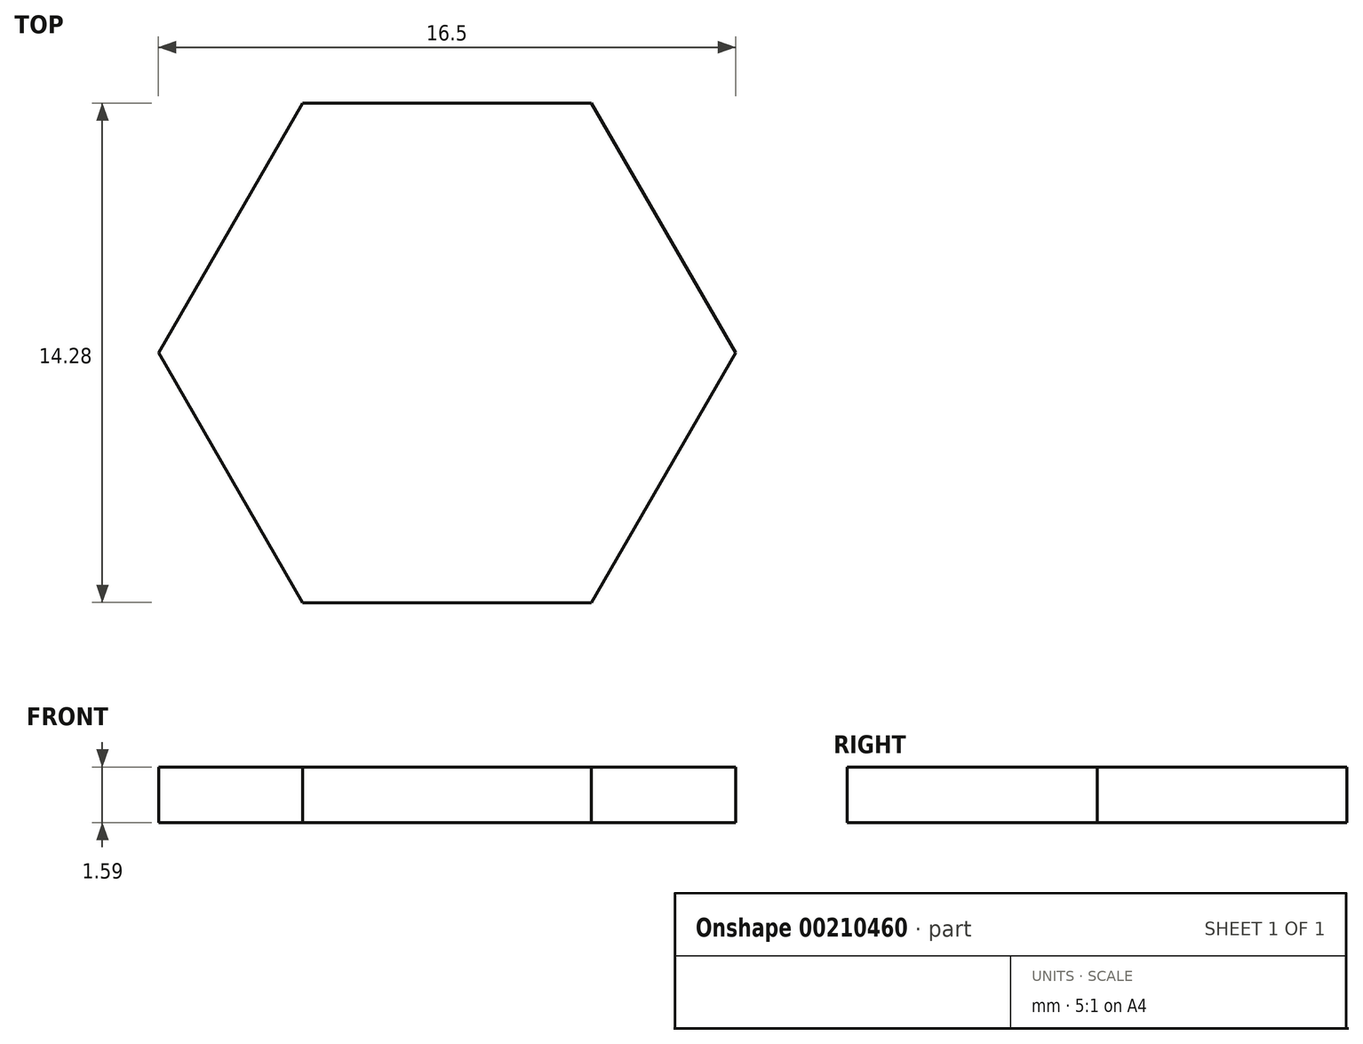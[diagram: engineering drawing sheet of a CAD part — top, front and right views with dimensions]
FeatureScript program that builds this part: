
annotation { "Feature Type Name" : "Feature", "Feature Type Description" : "" }
export const myFeature = defineFeature(function(context is Context, id is Id, definition is map)
    precondition{}
    {
        {
            var Q0;
            Q0=qCreatedBy(makeId("Top.planeOp"),FACE);
            var sketch = newSketch(context, id + "F0", { "sketchPlane" : qUnion([Q0])});
            skLineSegment(sketch, "E0.0", {"start": v(4.12, -7.14) * mm, "end": v(-4.12, -7.14) * mm});
            skLineSegment(sketch, "E0.1", {"start": v(-4.12, -7.14) * mm, "end": v(-8.25, 0) * mm});
            skLineSegment(sketch, "E0.2", {"start": v(-8.25, 0) * mm, "end": v(-4.12, 7.14) * mm});
            skLineSegment(sketch, "E0.3", {"start": v(-4.12, 7.14) * mm, "end": v(4.12, 7.14) * mm});
            skLineSegment(sketch, "E0.4", {"start": v(4.12, 7.14) * mm, "end": v(8.25, 0) * mm});
            skLineSegment(sketch, "E0.5", {"start": v(8.25, 0) * mm, "end": v(4.12, -7.14) * mm});
            skPoint(sketch, "E0.0.midPoint", {"position": v(0, -7.14) * mm});
            skSolve(sketch);
        }
        {
            var Q0;
            Q0=makeQuery(id+"F0.imprint","IMPRINT",FACE,{"disambiguationData":[TD([[makeQuery(id+"F0.imprint","IMPRINT",EDGE,{"derivedFrom":sQuery(id+"F0.wireOp",EDGE,"E0.0")}),-1.0]])]});
            extrude(context, id + "F1", {"entities" : qUnion([Q0]), "depth" : 1.59 * mm});
        }
    });
